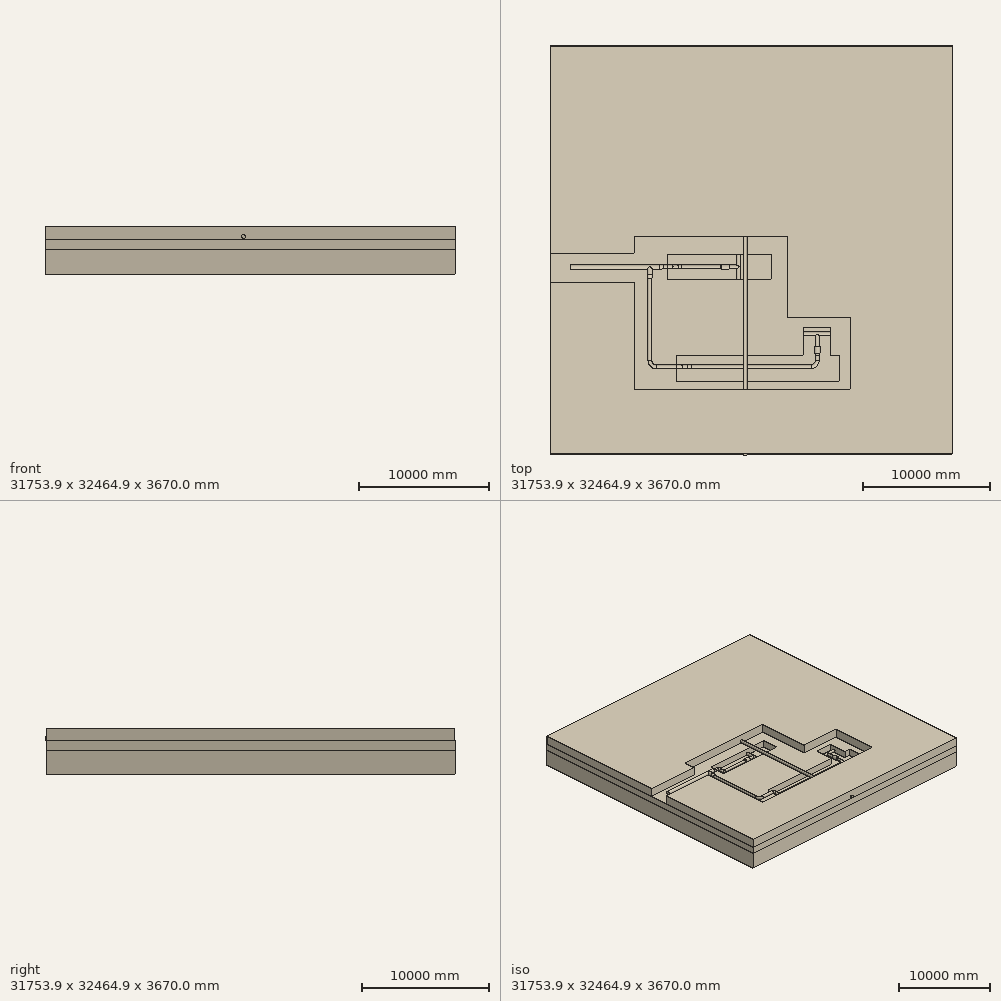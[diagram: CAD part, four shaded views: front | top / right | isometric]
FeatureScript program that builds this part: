
annotation { "Feature Type Name" : "Feature", "Feature Type Description" : "" }
export const myFeature = defineFeature(function(context is Context, id is Id, definition is map)
    precondition{}
    {
        {
            var Q0;
            Q0=qCreatedBy(makeId("Front.planeOp"),FACE);
            var sketch = newSketch(context, id + "F0", { "sketchPlane" : qUnion([Q0])});
            skCircle(sketch, "E0", {"center": v(0, 0) * mm, "radius": 157.5 * mm});
            skSolve(sketch);
        }
        {
            var Q0;
            Q0=qCreatedBy(makeId("Right.planeOp"),FACE);
            var sketch = newSketch(context, id + "F1", { "sketchPlane" : qUnion([Q0])});
            skLineSegment(sketch, "E1", {"start": v(0, 0) * mm, "end": v(-1158.97, 0) * mm});
            skLineSegment(sketch, "E2", {"start": v(-1512.52, -146.45) * mm, "end": v(-2019.63, -653.55) * mm});
            skLineSegment(sketch, "E3", {"start": v(-2373.18, -800) * mm, "end": v(-22166.07, -800) * mm});
            skPoint(sketch, "E4.visualSharp", {"position": v(-2166.07, -800) * mm});
            skArc(sketch, "E4.filletArc", {"start": v(-2373.18, -800) * mm, "mid": v(-2181.84, -761.94) * mm, "end": v(-2019.63, -653.55) * mm});
            skPoint(sketch, "E5.visualSharp", {"position": v(-1366.07, 0) * mm});
            skArc(sketch, "E5.filletArc", {"start": v(-1158.97, 0) * mm, "mid": v(-1350.3, -38.06) * mm, "end": v(-1512.52, -146.45) * mm});
            skSolve(sketch);
        }
        {
            var Q0;
            Q0 = qSketchRegion(id + "F0", true);
            var Q1;
            Q1 = qConstructionFilter(qBodyType(qCreatedBy(id + "F1" ,EDGE), BodyType.WIRE), ConstructionObject.NO);
            sweep(context, id + "F2", {"profiles" : qUnion([Q0]), "path" : qUnion([Q1])});
        }
        {
            var Q0;
            Q0=qCreatedBy(makeId("Front.planeOp"),FACE);
            var sketch = newSketch(context, id + "F3", { "sketchPlane" : qUnion([Q0])});
            skCircle(sketch, "E6", {"center": v(500, 0) * mm, "radius": 157.5 * mm});
            skSolve(sketch);
        }
        {
            var Q0;
            Q0 = qSketchRegion(id + "F3", true);
            extrude(context, id + "F4", {"entities" : qUnion([Q0]), "depth" : 31800 * mm, "offsetDistance" : 25 * mm});
        }
        {
            var Q0;
            Q0=qCreatedBy(makeId("Right.planeOp"),FACE);
            var sketch = newSketch(context, id + "F5", { "sketchPlane" : qUnion([Q0])});
            skCircle(sketch, "E7", {"center": v(-22166, -800) * mm, "radius": 157.5 * mm});
            skSolve(sketch);
        }
        {
            var Q0;
            Q0=qCreatedBy(makeId("Right.planeOp"),FACE);
            cPlane(context, id + "F6", {"entities" : qUnion([Q0]), "cplaneType" : CPlaneType.OFFSET, "offset" : 16000 * mm, "width" : 150 * mm, "height" : 150 * mm});
        }
        {
            var Q0;
            Q0=qCreatedBy(id+"F6.planeOp",FACE);
            var sketch = newSketch(context, id + "F7", { "sketchPlane" : qUnion([Q0])});
            skCircle(sketch, "E8", {"center": v(-21525.22, 0) * mm, "radius": 157.5 * mm});
            skSolve(sketch);
        }
        {
            var Q0;
            Q0=qCreatedBy(makeId("Front.planeOp"),FACE);
            var Q1;
            Q1=sQuery(id+"F7.wireOp",VERTEX,"E8.center");
            cPlane(context, id + "F8", {"entities" : qUnion([Q0, Q1]), "cplaneType" : CPlaneType.PLANE_POINT, "offset" : 25 * mm, "width" : 150 * mm, "height" : 150 * mm});
        }
        {
            var Q0;
            Q0=qCreatedBy(id+"F8.planeOp",FACE);
            var sketch = newSketch(context, id + "F9", { "sketchPlane" : qUnion([Q0])});
            skLineSegment(sketch, "E9", {"start": v(16002.5, 0) * mm, "end": v(14288.3, 0) * mm});
            skLineSegment(sketch, "E10", {"start": v(13967.3, -116.64) * mm, "end": v(12326.43, -1490.56) * mm});
            skLineSegment(sketch, "E11", {"start": v(12005.44, -1607.2) * mm, "end": v(-8115.68, -1607.2) * mm});
            skLineSegment(sketch, "E12", {"start": v(-8532.64, -1383.14) * mm, "end": v(-9299.71, -224.06) * mm});
            skLineSegment(sketch, "E13", {"start": v(-9716.67, 0) * mm, "end": v(-13355.66, 0) * mm});
            skPoint(sketch, "E14.visualSharp", {"position": v(14106.6, 0) * mm});
            skArc(sketch, "E14.filletArc", {"start": v(14288.3, 0) * mm, "mid": v(14117.53, -30.06) * mm, "end": v(13967.3, -116.64) * mm});
            skPoint(sketch, "E15.visualSharp", {"position": v(12187.13, -1607.2) * mm});
            skArc(sketch, "E15.filletArc", {"start": v(12005.44, -1607.2) * mm, "mid": v(12176.2, -1577.13) * mm, "end": v(12326.43, -1490.56) * mm});
            skPoint(sketch, "E16.visualSharp", {"position": v(-9448, 0) * mm});
            skArc(sketch, "E16.filletArc", {"start": v(-9299.71, -224.06) * mm, "mid": v(-9480, -59.56) * mm, "end": v(-9716.67, 0) * mm});
            skPoint(sketch, "E17.visualSharp", {"position": v(-8384.36, -1607.2) * mm});
            skArc(sketch, "E17.filletArc", {"start": v(-8532.64, -1383.14) * mm, "mid": v(-8352.35, -1547.63) * mm, "end": v(-8115.68, -1607.2) * mm});
            skSolve(sketch);
        }
        {
            var Q0;
            Q0 = qSketchRegion(id + "F7", true);
            var Q1;
            Q1 = qConstructionFilter(qBodyType(qCreatedBy(id + "F9" ,EDGE), BodyType.WIRE), ConstructionObject.NO);
            sweep(context, id + "F10", {"profiles" : qUnion([Q0]), "path" : qUnion([Q1])});
        }
        {
            var Q0;
            Q0=qCreatedBy(id+"F6.planeOp",FACE);
            var sketch = newSketch(context, id + "F11", { "sketchPlane" : qUnion([Q0])});
            skCircle(sketch, "E18", {"center": v(-22166, 0) * mm, "radius": 157.5 * mm});
            skSolve(sketch);
        }
        {
            var Q0;
            Q0=qCreatedBy(makeId("Front.planeOp"),FACE);
            var Q1;
            Q1=sQuery(id+"F11.wireOp",VERTEX,"E18.center");
            cPlane(context, id + "F12", {"entities" : qUnion([Q0, Q1]), "cplaneType" : CPlaneType.PLANE_POINT, "offset" : 25 * mm, "width" : 150 * mm, "height" : 150 * mm});
        }
        {
            var Q0;
            Q0=qCreatedBy(id+"F12.planeOp",FACE);
            var sketch = newSketch(context, id + "F13", { "sketchPlane" : qUnion([Q0])});
            skLineSegment(sketch, "E19", {"start": v(16049.86, 0) * mm, "end": v(14213.99, 0) * mm});
            skLineSegment(sketch, "E20", {"start": v(13860.44, -146.45) * mm, "end": v(13353.33, -653.55) * mm});
            skLineSegment(sketch, "E21", {"start": v(12999.78, -800) * mm, "end": v(0, -800) * mm});
            skLineSegment(sketch, "E22", {"start": v(0, -800) * mm, "end": v(-8588.31, -800) * mm});
            skLineSegment(sketch, "E23", {"start": v(-8941.87, -653.55) * mm, "end": v(-9448.97, -146.45) * mm});
            skLineSegment(sketch, "E24", {"start": v(-9802.53, 0) * mm, "end": v(-13399.06, 0) * mm});
            skPoint(sketch, "E25.visualSharp", {"position": v(14006.88, 0) * mm});
            skArc(sketch, "E25.filletArc", {"start": v(14213.99, 0) * mm, "mid": v(14022.65, -38.06) * mm, "end": v(13860.44, -146.45) * mm});
            skPoint(sketch, "E26.visualSharp", {"position": v(13206.88, -800) * mm});
            skArc(sketch, "E26.filletArc", {"start": v(12999.78, -800) * mm, "mid": v(13191.12, -761.94) * mm, "end": v(13353.33, -653.55) * mm});
            skPoint(sketch, "E27.visualSharp", {"position": v(-8795.42, -800) * mm});
            skArc(sketch, "E27.filletArc", {"start": v(-8941.87, -653.55) * mm, "mid": v(-8779.66, -761.94) * mm, "end": v(-8588.31, -800) * mm});
            skPoint(sketch, "E28.visualSharp", {"position": v(-9595.42, 0) * mm});
            skArc(sketch, "E28.filletArc", {"start": v(-9448.97, -146.45) * mm, "mid": v(-9611.19, -38.06) * mm, "end": v(-9802.53, 0) * mm});
            skSolve(sketch);
        }
        {
            var Q0;
            Q0 = qSketchRegion(id + "F11", true);
            var Q1;
            Q1 = qConstructionFilter(qBodyType(qCreatedBy(id + "F13" ,EDGE), BodyType.WIRE), ConstructionObject.NO);
            sweep(context, id + "F14", {"operationType" : NewBodyOperationType.ADD, "profiles" : qUnion([Q0]), "path" : qUnion([Q1])});
        }
        {
            var Q0;
            Q0=makeQuery(id+"F10.opSweep","CAP_FACE",FACE,{"disambiguationData":[OSD([sQuery(id+"F7.wireOp",EDGE,"E8"),sQuery(id+"F9.wireOp",VERTEX,"E13.end")])],"isStart":true});
            var sketch = newSketch(context, id + "F15", { "sketchPlane" : qUnion([Q0])});
            skCircle(sketch, "E29", {"center": v(16867.72, 0) * mm, "radius": 225 * mm});
            skSolve(sketch);
        }
        {
            var Q0;
            Q0 = qSketchRegion(id + "F15", true);
            extrude(context, id + "F16", {"entities" : qUnion([Q0]), "oppositeDirection" : true, "depth" : 7050 * mm, "offsetDistance" : 25 * mm});
        }
        {
            var Q0;
            Q0=makeQuery(id+"F16.opExtrude","CAP_FACE",FACE,{"disambiguationData":[OSD([sQuery(id+"F15.wireOp",EDGE,"E29")])],"isStart":false});
            var sketch = newSketch(context, id + "F17", { "sketchPlane" : qUnion([Q0])});
            skCircle(sketch, "E30", {"center": v(-16867.72, 0) * mm, "radius": 225 * mm});
            skSolve(sketch);
        }
        {
            var Q0;
            Q0=makeQuery(id+"F17.imprint","IMPRINT",FACE,{"disambiguationData":[TD([[makeQuery(id+"F17.imprint","IMPRINT",EDGE,{"derivedFrom":sQuery(id+"F17.wireOp",EDGE,"E30")}),-1.0]])]});
            cPlane(context, id + "F18", {"entities" : qUnion([Q0]), "cplaneType" : CPlaneType.OFFSET, "offset" : 343 * mm, "width" : 150 * mm, "height" : 150 * mm});
        }
        {
            var Q0;
            Q0=qCreatedBy(id+"F18.planeOp",FACE);
            var sketch = newSketch(context, id + "F19", { "sketchPlane" : qUnion([Q0])});
            skCircle(sketch, "E31", {"center": v(-16868.24, -67.5) * mm, "radius": 157.5 * mm});
            skSolve(sketch);
        }
        {
            var Q0;
            Q0 = qSketchRegion(id + "F17", true);
            var Q1;
            Q1 = qSketchRegion(id + "F19", true);
            loft(context, id + "F20", {"operationType" : NewBodyOperationType.ADD, "sheetProfilesArray" : [{ "sheetProfileEntities" : qUnion([Q0]) }, { "sheetProfileEntities" : qUnion([Q1]) }]});
        }
        {
            var Q0;
            Q0=qCreatedBy(makeId("Front.planeOp"),FACE);
            var Q1;
            Q1=sQuery(id+"F15.wireOp",VERTEX,"E29.center");
            cPlane(context, id + "F21", {"entities" : qUnion([Q0, Q1]), "cplaneType" : CPlaneType.PLANE_POINT, "offset" : 25 * mm, "width" : 150 * mm, "height" : 150 * mm});
        }
        {
            var Q0;
            Q0=qCreatedBy(id+"F21.planeOp",FACE);
            var sketch = newSketch(context, id + "F22", { "sketchPlane" : qUnion([Q0])});
            skLineSegment(sketch, "E32", {"start": v(-5962.66, -83.9) * mm, "end": v(-5669.76, -83.9) * mm});
            skLineSegment(sketch, "E33", {"start": v(-5316.21, -230.35) * mm, "end": v(-4893, -653.55) * mm});
            skLineSegment(sketch, "E34", {"start": v(-4539.45, -800) * mm, "end": v(-1450, -800) * mm});
            skPoint(sketch, "E35.visualSharp", {"position": v(-5462.66, -83.9) * mm});
            skArc(sketch, "E35.filletArc", {"start": v(-5316.21, -230.35) * mm, "mid": v(-5478.42, -121.96) * mm, "end": v(-5669.76, -83.9) * mm});
            skPoint(sketch, "E36.visualSharp", {"position": v(-4746.56, -800) * mm});
            skArc(sketch, "E36.filletArc", {"start": v(-4893, -653.55) * mm, "mid": v(-4730.8, -761.94) * mm, "end": v(-4539.45, -800) * mm});
            skSolve(sketch);
        }
        {
            var Q0;
            Q0 = qSketchRegion(id + "F19", true);
            var Q1;
            Q1 = qConstructionFilter(qBodyType(qCreatedBy(id + "F22" ,EDGE), BodyType.WIRE), ConstructionObject.NO);
            sweep(context, id + "F23", {"operationType" : NewBodyOperationType.ADD, "profiles" : qUnion([Q0]), "path" : qUnion([Q1])});
        }
        {
            var Q0;
            Q0=makeQuery(id+"F23.opSweep","CAP_FACE",FACE,{"disambiguationData":[OSD([sQuery(id+"F19.wireOp",EDGE,"E31"),sQuery(id+"F22.wireOp",VERTEX,"E34.end")])],"isStart":false});
            var sketch = newSketch(context, id + "F24", { "sketchPlane" : qUnion([Q0])});
            skCircle(sketch, "E37", {"center": v(-16868.24, -783.6) * mm, "radius": 157.5 * mm});
            skSolve(sketch);
        }
        {
            var Q0;
            Q0=qCreatedBy(makeId("Front.planeOp"),FACE);
            var Q1;
            Q1=sQuery(id+"F24.wireOp",VERTEX,"E37.center");
            cPlane(context, id + "F25", {"entities" : qUnion([Q0, Q1]), "cplaneType" : CPlaneType.PLANE_POINT, "offset" : 25 * mm, "width" : 150 * mm, "height" : 150 * mm});
        }
        {
            var Q0;
            Q0=qCreatedBy(id+"F25.planeOp",FACE);
            var sketch = newSketch(context, id + "F26", { "sketchPlane" : qUnion([Q0])});
            skCircle(sketch, "E38", {"center": v(-7026.1, 0) * mm, "radius": 225 * mm});
            skSolve(sketch);
        }
        {
            var Q0;
            Q0 = qSketchRegion(id + "F26", true);
            extrude(context, id + "F27", {"entities" : qUnion([Q0]), "operationType" : NewBodyOperationType.ADD, "depth" : 610 * mm, "offsetDistance" : 25 * mm});
        }
        {
            var Q0;
            Q0=makeQuery(id+"F27.opExtrude","CAP_FACE",FACE,{"disambiguationData":[OSD([sQuery(id+"F26.wireOp",EDGE,"E38")])],"isStart":false});
            var sketch = newSketch(context, id + "F28", { "sketchPlane" : qUnion([Q0])});
            skCircle(sketch, "E39", {"center": v(-7026.1, 0) * mm, "radius": 225 * mm});
            skSolve(sketch);
        }
        {
            var Q0;
            Q0=makeQuery(id+"F28.imprint","IMPRINT",FACE,{"disambiguationData":[TD([[makeQuery(id+"F28.imprint","IMPRINT",EDGE,{"derivedFrom":sQuery(id+"F28.wireOp",EDGE,"E39")}),1.0]])]});
            cPlane(context, id + "F29", {"entities" : qUnion([Q0]), "cplaneType" : CPlaneType.OFFSET, "offset" : 300 * mm, "width" : 150 * mm, "height" : 150 * mm});
        }
        {
            var Q0;
            Q0=qCreatedBy(id+"F29.planeOp",FACE);
            var sketch = newSketch(context, id + "F30", { "sketchPlane" : qUnion([Q0])});
            skCircle(sketch, "E40", {"center": v(-7026.1, -68) * mm, "radius": 157.5 * mm});
            skSolve(sketch);
        }
        {
            var Q0;
            Q0 = qSketchRegion(id + "F28", true);
            var Q1;
            Q1 = qSketchRegion(id + "F30", true);
            loft(context, id + "F31", {"operationType" : NewBodyOperationType.ADD, "sheetProfilesArray" : [{ "sheetProfileEntities" : qUnion([Q0]) }, { "sheetProfileEntities" : qUnion([Q1]) }]});
        }
        {
            var Q0;
            Q0=qCreatedBy(id+"F29.planeOp",FACE);
            var sketch = newSketch(context, id + "F32", { "sketchPlane" : qUnion([Q0])});
            skCircle(sketch, "E41", {"center": v(-7028.94, -67.68) * mm, "radius": 157.5 * mm});
            skSolve(sketch);
        }
        {
            var Q0;
            Q0 = qSketchRegion(id + "F30", true);
            extrude(context, id + "F33", {"entities" : qUnion([Q0]), "operationType" : NewBodyOperationType.ADD, "depth" : 5500 * mm, "offsetDistance" : 25 * mm});
        }
        {
            var Q0;
            Q0=qCreatedBy(makeId("Top.planeOp"),FACE);
            var Q1;
            Q1=sQuery(id+"F32.wireOp",VERTEX,"E41.center");
            cPlane(context, id + "F34", {"entities" : qUnion([Q0, Q1]), "cplaneType" : CPlaneType.PLANE_POINT, "offset" : 25 * mm, "width" : 150 * mm, "height" : 150 * mm});
        }
        {
            var Q0;
            Q0=qCreatedBy(id+"F34.planeOp",FACE);
            var sketch = newSketch(context, id + "F35", { "sketchPlane" : qUnion([Q0])});
            skLineSegment(sketch, "E42", {"start": v(-7028.94, -23278.24) * mm, "end": v(-7028.94, -24278.24) * mm});
            skLineSegment(sketch, "E43", {"start": v(-6528.94, -24778.24) * mm, "end": v(-5528.94, -24778.24) * mm});
            skPoint(sketch, "E44.visualSharp", {"position": v(-7028.94, -24778.24) * mm});
            skArc(sketch, "E44.filletArc", {"start": v(-7028.94, -24278.24) * mm, "mid": v(-6882.49, -24631.79) * mm, "end": v(-6528.94, -24778.24) * mm});
            skSolve(sketch);
        }
        {
            var Q0;
            Q0=makeQuery(id+"F33.opExtrude","CAP_FACE",FACE,{"disambiguationData":[OSD([sQuery(id+"F30.wireOp",EDGE,"E40")])],"isStart":false});
            var sketch = newSketch(context, id + "F36", { "sketchPlane" : qUnion([Q0])});
            skCircle(sketch, "E45", {"center": v(-7026.1, -68) * mm, "radius": 157.5 * mm});
            skSolve(sketch);
        }
        {
            var Q0;
            Q0 = qSketchRegion(id + "F36", true);
            var Q1;
            Q1 = qConstructionFilter(qBodyType(qCreatedBy(id + "F35" ,EDGE), BodyType.WIRE), ConstructionObject.NO);
            sweep(context, id + "F37", {"operationType" : NewBodyOperationType.ADD, "profiles" : qUnion([Q0]), "path" : qUnion([Q1])});
        }
        {
            var Q0;
            Q0=makeQuery(id+"F37.opSweep","CAP_FACE",FACE,{"disambiguationData":[OSD([sQuery(id+"F35.wireOp",VERTEX,"E43.end"),sQuery(id+"F36.wireOp",EDGE,"E45")])],"isStart":false});
            var sketch = newSketch(context, id + "F38", { "sketchPlane" : qUnion([Q0])});
            skCircle(sketch, "E46", {"center": v(-24775.4, -68) * mm, "radius": 157.5 * mm});
            skSolve(sketch);
        }
        {
            var Q0;
            Q0=qCreatedBy(makeId("Front.planeOp"),FACE);
            var Q1;
            Q1=sQuery(id+"F38.wireOp",VERTEX,"E46.center");
            cPlane(context, id + "F39", {"entities" : qUnion([Q0, Q1]), "cplaneType" : CPlaneType.PLANE_POINT, "offset" : 25 * mm, "width" : 150 * mm, "height" : 150 * mm});
        }
        {
            var Q0;
            Q0=qCreatedBy(id+"F39.planeOp",FACE);
            var sketch = newSketch(context, id + "F40", { "sketchPlane" : qUnion([Q0])});
            skLineSegment(sketch, "E47", {"start": v(-5528.94, -67.68) * mm, "end": v(-4920.36, -67.68) * mm});
            skLineSegment(sketch, "E48", {"start": v(-4566.8, -214.12) * mm, "end": v(-4127.37, -653.55) * mm});
            skLineSegment(sketch, "E49", {"start": v(-3773.82, -800) * mm, "end": v(4519.07, -800) * mm});
            skPoint(sketch, "E50.visualSharp", {"position": v(-4713.25, -67.68) * mm});
            skArc(sketch, "E50.filletArc", {"start": v(-4566.8, -214.12) * mm, "mid": v(-4729.02, -105.74) * mm, "end": v(-4920.36, -67.68) * mm});
            skPoint(sketch, "E51.visualSharp", {"position": v(-3980.93, -800) * mm});
            skArc(sketch, "E51.filletArc", {"start": v(-4127.37, -653.55) * mm, "mid": v(-3965.16, -761.94) * mm, "end": v(-3773.82, -800) * mm});
            skSolve(sketch);
        }
        {
            var Q0;
            Q0 = qSketchRegion(id + "F38", true);
            var Q1;
            Q1 = qConstructionFilter(qBodyType(qCreatedBy(id + "F40" ,EDGE), BodyType.WIRE), ConstructionObject.NO);
            sweep(context, id + "F41", {"operationType" : NewBodyOperationType.ADD, "profiles" : qUnion([Q0]), "path" : qUnion([Q1])});
        }
        {
            var Q0;
            Q0=makeQuery(id+"F41.opSweep","CAP_FACE",FACE,{"disambiguationData":[OSD([sQuery(id+"F38.wireOp",EDGE,"E46"),sQuery(id+"F40.wireOp",VERTEX,"E49.end")])],"isStart":false});
            var sketch = newSketch(context, id + "F42", { "sketchPlane" : qUnion([Q0])});
            skCircle(sketch, "E52", {"center": v(-24775.4, -800.32) * mm, "radius": 157.5 * mm});
            skSolve(sketch);
        }
        {
            var Q0;
            Q0=qCreatedBy(makeId("Top.planeOp"),FACE);
            var Q1;
            Q1=sQuery(id+"F42.wireOp",VERTEX,"E52.center");
            cPlane(context, id + "F43", {"entities" : qUnion([Q0, Q1]), "cplaneType" : CPlaneType.PLANE_POINT, "offset" : 25 * mm, "width" : 150 * mm, "height" : 150 * mm});
        }
        {
            var Q0;
            Q0=qCreatedBy(id+"F43.planeOp",FACE);
            var sketch = newSketch(context, id + "F44", { "sketchPlane" : qUnion([Q0])});
            skLineSegment(sketch, "E53", {"start": v(4519.07, -24775.4) * mm, "end": v(5727.78, -24775.4) * mm});
            skLineSegment(sketch, "E54", {"start": v(6227.78, -24275.4) * mm, "end": v(6227.78, -23859.04) * mm});
            skPoint(sketch, "E55.visualSharp", {"position": v(6227.78, -24775.4) * mm});
            skArc(sketch, "E55.filletArc", {"start": v(5727.78, -24775.4) * mm, "mid": v(6081.34, -24628.95) * mm, "end": v(6227.78, -24275.4) * mm});
            skSolve(sketch);
        }
        {
            var Q0;
            Q0 = qSketchRegion(id + "F42", true);
            var Q1;
            Q1 = qConstructionFilter(qBodyType(qCreatedBy(id + "F44" ,EDGE), BodyType.WIRE), ConstructionObject.NO);
            sweep(context, id + "F45", {"operationType" : NewBodyOperationType.ADD, "profiles" : qUnion([Q0]), "path" : qUnion([Q1])});
        }
        {
            var Q0;
            Q0=makeQuery(id+"F24.imprint","IMPRINT",FACE,{"disambiguationData":[TD([[makeQuery(id+"F24.imprint","IMPRINT",EDGE,{"derivedFrom":sQuery(id+"F24.wireOp",EDGE,"E37")}),1.0]])]});
            var sketch = newSketch(context, id + "F46", { "sketchPlane" : qUnion([Q0])});
            skCircle(sketch, "E56", {"center": v(-16868.23, -783.6) * mm, "radius": 157.5 * mm});
            skSolve(sketch);
        }
        {
            var Q0;
            Q0 = qSketchRegion(id + "F46", true);
            extrude(context, id + "F47", {"entities" : qUnion([Q0]), "depth" : 120 * mm, "offsetDistance" : 25 * mm});
        }
        {
            var Q0;
            Q0=makeQuery(id+"F47.opExtrude","CAP_FACE",FACE,{"disambiguationData":[OSD([sQuery(id+"F46.wireOp",EDGE,"E56")])],"isStart":false});
            var sketch = newSketch(context, id + "F48", { "sketchPlane" : qUnion([Q0])});
            skCircle(sketch, "E57", {"center": v(-16868.23, -783.6) * mm, "radius": 225 * mm});
            skSolve(sketch);
        }
        {
            var Q0;
            Q0 = qSketchRegion(id + "F48", true);
            extrude(context, id + "F49", {"entities" : qUnion([Q0]), "operationType" : NewBodyOperationType.ADD, "depth" : 610 * mm, "offsetDistance" : 25 * mm});
        }
        {
            var Q0;
            Q0=makeQuery(id+"F49.opExtrude","CAP_FACE",FACE,{"disambiguationData":[OSD([sQuery(id+"F48.wireOp",EDGE,"E57")])],"isStart":false});
            var sketch = newSketch(context, id + "F50", { "sketchPlane" : qUnion([Q0])});
            skCircle(sketch, "E58", {"center": v(-16868.23, -783.6) * mm, "radius": 157.5 * mm});
            skSolve(sketch);
        }
        {
            var Q0;
            Q0 = qSketchRegion(id + "F50", true);
            var Q1;
            {var subQ0=sQuery(id+"F0.wireOp",EDGE,"E0");var subQ1=makeQuery(id+"F2.opSweep","SWEPT_FACE",FACE,{"disambiguationData":[OSD([subQ0,sQuery(id+"F1.wireOp",EDGE,"E3")])]});Q1=makeQuery(id+"F14.boolean.opBoolean","SPLIT",FACE,{"disambiguationData":[TD([subQ1,makeQuery(id+"F2.opSweep","SWEPT_FACE",FACE,{"disambiguationData":[OSD([subQ0,sQuery(id+"F1.wireOp",EDGE,"E4.filletArc")])]}),makeQuery(id+"F14.opSweep","SWEPT_FACE",FACE,{"disambiguationData":[OSD([sQuery(id+"F11.wireOp",EDGE,"E18"),sQuery(id+"F13.wireOp",EDGE,"E22")])]})])],"derivedFrom":subQ1});}
            extrude(context, id + "F51", {"entities" : qUnion([Q0]), "depth" : 770 * mm, "endBoundEntityFace" : qUnion([Q1]), "offsetDistance" : 25 * mm});
        }
        {
            var Q0;
            Q0=qCreatedBy(makeId("Top.planeOp"),FACE);
            cPlane(context, id + "F52", {"entities" : qUnion([Q0]), "cplaneType" : CPlaneType.OFFSET, "offset" : 2900 * mm, "oppositeDirection" : true, "width" : 150 * mm, "height" : 150 * mm});
        }
        {
            var Q0;
            Q0=qCreatedBy(id+"F52.planeOp",FACE);
            var sketch = newSketch(context, id + "F53", { "sketchPlane" : qUnion([Q0])});
            skLineSegment(sketch, "E59.bottom", {"start": v(-14864.21, 664.91) * mm, "end": v(16889.7, 664.91) * mm});
            skLineSegment(sketch, "E59.top", {"start": v(-14864.21, -31680.33) * mm, "end": v(16889.7, -31680.33) * mm});
            skLineSegment(sketch, "E59.left", {"start": v(-14864.21, 664.91) * mm, "end": v(-14864.21, -31680.33) * mm});
            skLineSegment(sketch, "E59.right", {"start": v(16889.7, 664.91) * mm, "end": v(16889.7, -31680.33) * mm});
            skSolve(sketch);
        }
        {
            var Q0;
            Q0=makeQuery(id+"F45.opSweep","CAP_FACE",FACE,{"disambiguationData":[OSD([sQuery(id+"F42.wireOp",EDGE,"E52"),sQuery(id+"F44.wireOp",VERTEX,"E54.end")])],"isStart":false});
            var sketch = newSketch(context, id + "F54", { "sketchPlane" : qUnion([Q0])});
            skCircle(sketch, "E60", {"center": v(-6227.78, -800.32) * mm, "radius": 157.5 * mm});
            skSolve(sketch);
        }
        {
            var Q0;
            Q0 = qSketchRegion(id + "F54", true);
            extrude(context, id + "F55", {"entities" : qUnion([Q0]), "depth" : 110 * mm, "offsetDistance" : 25 * mm});
        }
        {
            var Q0;
            Q0=makeQuery(id+"F55.opExtrude","CAP_FACE",FACE,{"disambiguationData":[OSD([sQuery(id+"F54.wireOp",EDGE,"E60")])],"isStart":false});
            var sketch = newSketch(context, id + "F56", { "sketchPlane" : qUnion([Q0])});
            skCircle(sketch, "E61", {"center": v(-6227.78, -800.32) * mm, "radius": 225 * mm});
            skSolve(sketch);
        }
        {
            var Q0;
            Q0 = qSketchRegion(id + "F56", true);
            extrude(context, id + "F57", {"entities" : qUnion([Q0]), "operationType" : NewBodyOperationType.ADD, "depth" : 560 * mm, "offsetDistance" : 25 * mm});
        }
        {
            var Q0;
            Q0=makeQuery(id+"F57.opExtrude","CAP_FACE",FACE,{"disambiguationData":[OSD([sQuery(id+"F56.wireOp",EDGE,"E61")])],"isStart":false});
            var sketch = newSketch(context, id + "F58", { "sketchPlane" : qUnion([Q0])});
            skCircle(sketch, "E62", {"center": v(-6227.78, -800.32) * mm, "radius": 157.5 * mm});
            skSolve(sketch);
        }
        {
            var Q0;
            Q0 = qSketchRegion(id + "F58", true);
            extrude(context, id + "F59", {"entities" : qUnion([Q0]), "depth" : 1000 * mm, "offsetDistance" : 25 * mm});
        }
        {
            var Q0;
            Q0 = qSketchRegion(id + "F53", true);
            extrude(context, id + "F60", {"entities" : qUnion([Q0]), "depth" : 1890 * mm, "offsetDistance" : 25 * mm});
        }
        {
            var Q0;
            Q0=makeQuery(id+"F60.opExtrude","CAP_FACE",FACE,{"disambiguationData":[OSD([sQuery(id+"F53.wireOp",EDGE,"E59.bottom"),sQuery(id+"F53.wireOp",EDGE,"E59.top"),sQuery(id+"F53.wireOp",EDGE,"E59.left"),sQuery(id+"F53.wireOp",EDGE,"E59.right")])],"isStart":false});
            var sketch = newSketch(context, id + "F61", { "sketchPlane" : qUnion([Q0])});
            skLineSegment(sketch, "E63.bottom", {"start": v(-14864.21, 664.91) * mm, "end": v(16889.7, 664.91) * mm});
            skLineSegment(sketch, "E63.top", {"start": v(-5631.58, -15868.24) * mm, "end": v(2598.27, -15868.24) * mm});
            skLineSegment(sketch, "E63.left", {"start": v(-14864.21, 664.91) * mm, "end": v(-14864.21, -15868.24) * mm});
            skLineSegment(sketch, "E63.right", {"start": v(16889.7, 664.91) * mm, "end": v(16889.7, -15868.24) * mm});
            skLineSegment(sketch, "E64.top", {"start": v(-14864.21, -31680.33) * mm, "end": v(16889.7, -31680.33) * mm});
            skLineSegment(sketch, "E64.left", {"start": v(-14864.21, -15868.24) * mm, "end": v(-14864.21, -31680.33) * mm});
            skLineSegment(sketch, "E64.right", {"start": v(16889.7, -15868.24) * mm, "end": v(16889.7, -31680.33) * mm});
            skLineSegment(sketch, "E65.bottom", {"start": v(-4915.26, -23875.4) * mm, "end": v(5162.32, -23875.4) * mm});
            skLineSegment(sketch, "E65.right", {"start": v(7996.1, -23875.4) * mm, "end": v(7996.1, -25962.14) * mm});
            skLineSegment(sketch, "E66.bottom", {"start": v(5162.32, -21640.6) * mm, "end": v(7275.16, -21640.6) * mm});
            skLineSegment(sketch, "E66.left", {"start": v(5162.32, -21640.6) * mm, "end": v(5162.32, -23875.4) * mm});
            skLineSegment(sketch, "E66.right", {"start": v(7275.16, -21640.6) * mm, "end": v(7275.16, -23875.4) * mm});
            skLineSegment(sketch, "E67.trimOffspring", {"start": v(7275.16, -23875.4) * mm, "end": v(7996.1, -23875.4) * mm});
            skLineSegment(sketch, "E68.trimOffspring", {"start": v(-5631.58, -17868.24) * mm, "end": v(2598.27, -17868.24) * mm});
            skLineSegment(sketch, "E69", {"start": v(-4915.26, -23875.4) * mm, "end": v(-4915.26, -25962.14) * mm});
            skLineSegment(sketch, "E70.trimOffspring", {"start": v(-4915.26, -25962.14) * mm, "end": v(7996.1, -25962.14) * mm});
            skLineSegment(sketch, "E71", {"start": v(-5631.58, -17868.24) * mm, "end": v(-5631.58, -15868.24) * mm});
            skLineSegment(sketch, "E72", {"start": v(2598.27, -17868.24) * mm, "end": v(2598.27, -15868.24) * mm});
            skSolve(sketch);
        }
        {
            var Q0;
            Q0 = qSketchRegion(id + "F61", true);
            extrude(context, id + "F62", {"entities" : qUnion([Q0]), "depth" : 780 * mm, "offsetDistance" : 25 * mm});
        }
        {
            var Q0;
            Q0=makeQuery(id+"F62.opExtrude","CAP_FACE",FACE,{"disambiguationData":[OSD([sQuery(id+"F61.wireOp",EDGE,"E63.bottom"),sQuery(id+"F61.wireOp",EDGE,"E63.top"),sQuery(id+"F61.wireOp",EDGE,"E63.left"),sQuery(id+"F61.wireOp",EDGE,"E63.right"),sQuery(id+"F61.wireOp",EDGE,"E64.top"),sQuery(id+"F61.wireOp",EDGE,"E64.left"),sQuery(id+"F61.wireOp",EDGE,"E64.right"),sQuery(id+"F61.wireOp",EDGE,"E65.bottom"),sQuery(id+"F61.wireOp",EDGE,"E65.right"),sQuery(id+"F61.wireOp",EDGE,"E66.bottom"),sQuery(id+"F61.wireOp",EDGE,"E66.left"),sQuery(id+"F61.wireOp",EDGE,"E66.right"),sQuery(id+"F61.wireOp",EDGE,"E67.trimOffspring"),sQuery(id+"F61.wireOp",EDGE,"E68.trimOffspring"),sQuery(id+"F61.wireOp",EDGE,"E69"),sQuery(id+"F61.wireOp",EDGE,"E70.trimOffspring"),sQuery(id+"F61.wireOp",EDGE,"E71"),sQuery(id+"F61.wireOp",EDGE,"E72")])],"isStart":false});
            var sketch = newSketch(context, id + "F63", { "sketchPlane" : qUnion([Q0])});
            skLineSegment(sketch, "E73.bottom", {"start": v(-14864.21, 583.74) * mm, "end": v(16889.7, 583.74) * mm});
            skLineSegment(sketch, "E73.top", {"start": v(-8262.13, -14419.15) * mm, "end": v(3854.96, -14419.15) * mm});
            skLineSegment(sketch, "E73.left", {"start": v(-14864.21, 583.74) * mm, "end": v(-14864.21, -15805.74) * mm});
            skLineSegment(sketch, "E73.right", {"start": v(16889.7, 583.74) * mm, "end": v(16889.7, -14419.15) * mm});
            skLineSegment(sketch, "E74.bottom", {"start": v(-14864.21, -18097.1) * mm, "end": v(-8262.13, -18097.1) * mm});
            skLineSegment(sketch, "E74.left", {"start": v(-14864.21, -18097.1) * mm, "end": v(-14864.21, -26594.84) * mm});
            skLineSegment(sketch, "E75", {"start": v(-8262.13, -18097.1) * mm, "end": v(-8262.13, -26594.84) * mm});
            skLineSegment(sketch, "E76.bottom", {"start": v(-14864.21, -31680.33) * mm, "end": v(16889.7, -31680.33) * mm});
            skLineSegment(sketch, "E76.top", {"start": v(-14864.21, -26594.84) * mm, "end": v(8837.54, -26594.84) * mm});
            skLineSegment(sketch, "E76.left", {"start": v(-14864.21, -31680.33) * mm, "end": v(-14864.21, -26594.84) * mm});
            skLineSegment(sketch, "E76.right", {"start": v(16889.7, -31680.33) * mm, "end": v(16889.7, -26594.84) * mm});
            skLineSegment(sketch, "E77.left", {"start": v(16889.7, -14419.15) * mm, "end": v(16889.7, -26594.84) * mm});
            skLineSegment(sketch, "E77.right", {"start": v(8837.54, -20900.91) * mm, "end": v(8837.54, -26594.84) * mm});
            skLineSegment(sketch, "E78.top", {"start": v(3854.96, -20900.91) * mm, "end": v(8837.54, -20900.91) * mm});
            skLineSegment(sketch, "E78.left", {"start": v(3854.96, -14419.15) * mm, "end": v(3854.96, -20900.91) * mm});
            skLineSegment(sketch, "E79.top", {"start": v(-8262.13, -15805.74) * mm, "end": v(-14864.21, -15805.74) * mm});
            skLineSegment(sketch, "E79.left", {"start": v(-8262.13, -14419.15) * mm, "end": v(-8262.13, -15805.74) * mm});
            skSolve(sketch);
        }
        {
            var Q0;
            Q0 = qSketchRegion(id + "F63", true);
            extrude(context, id + "F64", {"entities" : qUnion([Q0]), "depth" : 1000 * mm, "offsetDistance" : 25 * mm});
        }
    });
